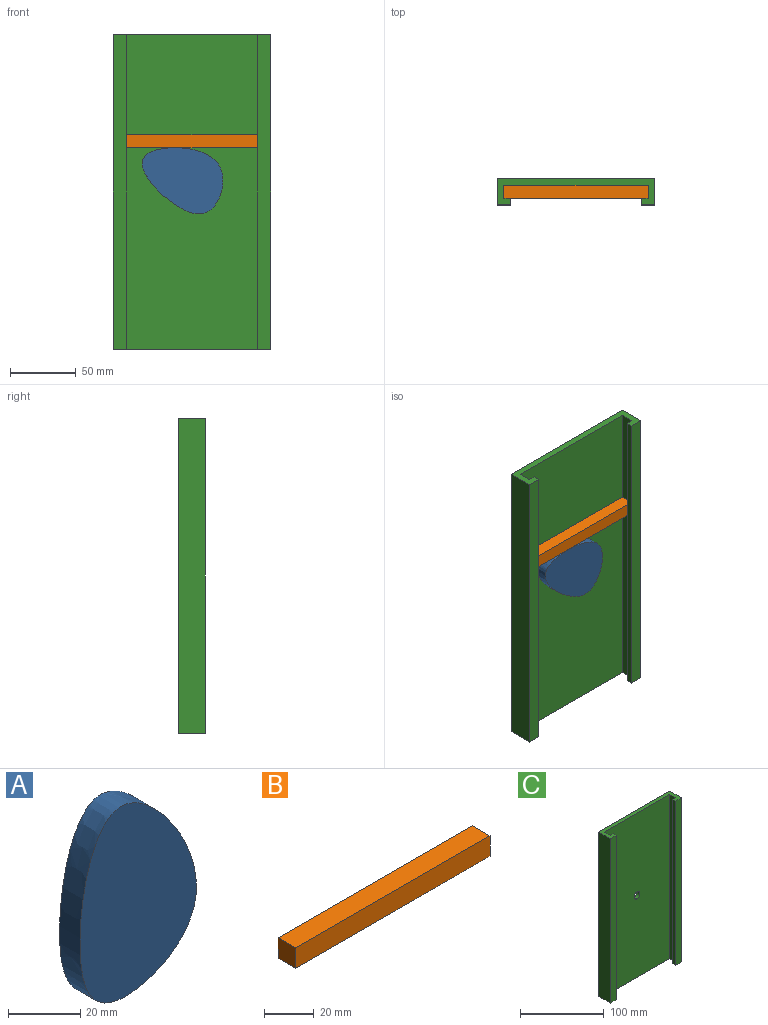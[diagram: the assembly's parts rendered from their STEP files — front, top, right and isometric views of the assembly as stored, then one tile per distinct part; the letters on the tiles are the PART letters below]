
ASSEMBLY  parts=3 mates=2
PART A: 5 faces, bbox 51x15x69 mm
  f0: plane 10x10mm, normal (0,1,0), area 78.5mm2, adj f1
  f1: cylinder r=5mm len=10mm, axis (0,-1,0), area 219.9mm2, adj f0,f4
  f2: extruded ~65.1x45.46mm, area 1405.8mm2, adj f3,f4
  f3: plane 69.02x51.05mm, normal (0,-1,0), area 2271.9mm2, adj f2
  f4: plane 69.02x51.05mm, normal (0,1,0), area 2193.4mm2, adj f1,f2
PART B: 6 faces, bbox 110x10x10 mm
  f0: plane 10x10mm, normal (1,0,0), area 100mm2, adj f1,f2,f4,f5
  f1: plane 110x10mm, normal (0,0,1), area 1100mm2, adj f0,f3,f4,f5
  f2: plane 110x10mm, normal (0,0,-1), area 1100mm2, adj f0,f3,f4,f5
  f3: plane 10x10mm, normal (-1,0,0), area 100mm2, adj f1,f2,f4,f5
  f4: plane 110x10mm, normal (0,1,0), area 1100mm2, adj f0,f1,f2,f3
  f5: plane 110x10mm, normal (0,-1,0), area 1100mm2, adj f0,f1,f2,f3
PART C: 15 faces, bbox 120x20x240 mm
  f0: plane 240x5mm, normal (1,0,0), area 1200mm2, adj f1,f3,f8,f13
  f1: plane 120x20mm, normal (0,0,-1), area 800mm2, adj f0,f2,f4,f5,f6,f7,f8,f9
  f2: plane 240x5mm, normal (-1,0,0), area 1200mm2, adj f1,f3,f6,f11
  f3: plane 120x20mm, normal (0,0,1), area 800mm2, adj f0,f2,f4,f5,f6,f7,f8,f9
  f4: plane 240x110mm, normal (0,-1,0), area 26321.5mm2, adj f1,f3,f5,f7,f14
  f5: plane 240x10mm, normal (-1,0,0), area 2400mm2, adj f1,f3,f4,f6
  f6: plane 240x5mm, normal (0,1,0), area 1200mm2, adj f1,f2,f3,f5
  f7: plane 240x10mm, normal (1,0,0), area 2400mm2, adj f1,f3,f4,f8
  f8: plane 240x5mm, normal (0,1,0), area 1200mm2, adj f0,f1,f3,f7
  f9: plane 240x120mm, normal (0,1,0), area 28721.5mm2, adj f1,f3,f10,f12,f14
  f10: plane 240x20mm, normal (1,0,0), area 4800mm2, adj f1,f3,f9,f11
  f11: plane 240x10mm, normal (0,-1,0), area 2400mm2, adj f1,f2,f3,f10
  f12: plane 240x20mm, normal (-1,0,0), area 4800mm2, adj f1,f3,f9,f13
  f13: plane 240x10mm, normal (0,-1,0), area 2400mm2, adj f0,f1,f3,f12
  f14: cylinder r=5mm len=10mm, axis (0,-1,0), area 157.1mm2, adj f4,f9
PLACE A rot(axis=(0,-1,0),54.9deg) t=(-143.03,0,-93.04)mm
PLACE B t=(-74.07,0,-71)mm
PLACE C t=(-74.07,0,5.17)mm fixed
MATE slider C.f3 <-> B.f1  axis (0,0,1) through (-129.07,2,125.17)mm
MATE revolute A.f1 <-> C.f14  axis (0,1,0) through (-74.07,7,5.17)mm
